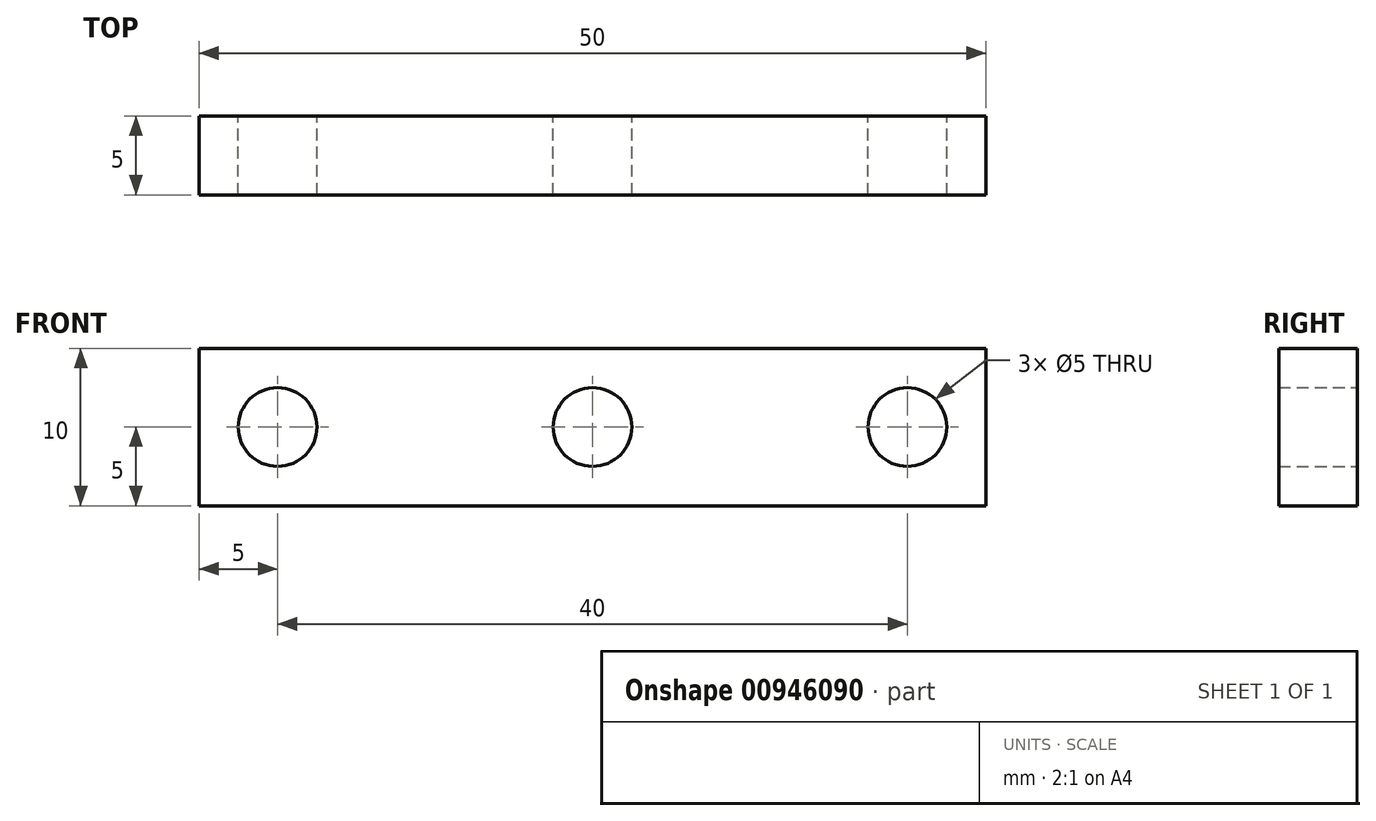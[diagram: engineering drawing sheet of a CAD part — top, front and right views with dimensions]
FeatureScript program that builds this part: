
annotation { "Feature Type Name" : "Feature", "Feature Type Description" : "" }
export const myFeature = defineFeature(function(context is Context, id is Id, definition is map)
    precondition{}
    {
        {
            var Q0;
            Q0=qCreatedBy(makeId("Front.planeOp"),FACE);
            var sketch = newSketch(context, id + "F0", { "sketchPlane" : qUnion([Q0])});
            skLineSegment(sketch, "E0.bottom", {"start": v(25, -5) * mm, "end": v(-25, -5) * mm});
            skLineSegment(sketch, "E0.top", {"start": v(25, 5) * mm, "end": v(-25, 5) * mm});
            skLineSegment(sketch, "E0.left", {"start": v(25, -5) * mm, "end": v(25, 5) * mm});
            skLineSegment(sketch, "E0.right", {"start": v(-25, -5) * mm, "end": v(-25, 5) * mm});
            skPoint(sketch, "E0.middle", {"position": v(0, 0) * mm});
            skSolve(sketch);
        }
        {
            var Q0;
            Q0=makeQuery(id+"F0.imprint","IMPRINT",FACE,{"disambiguationData":[TD([[makeQuery(id+"F0.imprint","IMPRINT",EDGE,{"derivedFrom":sQuery(id+"F0.wireOp",EDGE,"E0.bottom")}),-1.0]])]});
            var sketch = newSketch(context, id + "F1", { "sketchPlane" : qUnion([Q0])});
            skCircle(sketch, "E1", {"center": v(0, 0) * mm, "radius": 2.5 * mm});
            skCircle(sketch, "E2", {"center": v(-20, 0) * mm, "radius": 2.5 * mm});
            skCircle(sketch, "E3", {"center": v(20, 0) * mm, "radius": 2.5 * mm});
            skSolve(sketch);
        }
        {
            var Q0;
            Q0=makeQuery(id+"F1.imprint","IMPRINT",FACE,{"disambiguationData":[TD([[makeQuery(id+"F1.imprint","IMPRINT",EDGE,{"derivedFrom":sQuery(id+"F1.wireOp",EDGE,"E1")}),-1.0]])]});
            extrude(context, id + "F2", {"entities" : qUnion([Q0]), "depth" : 5 * mm, "offsetDistance" : 25 * mm});
        }
    });
